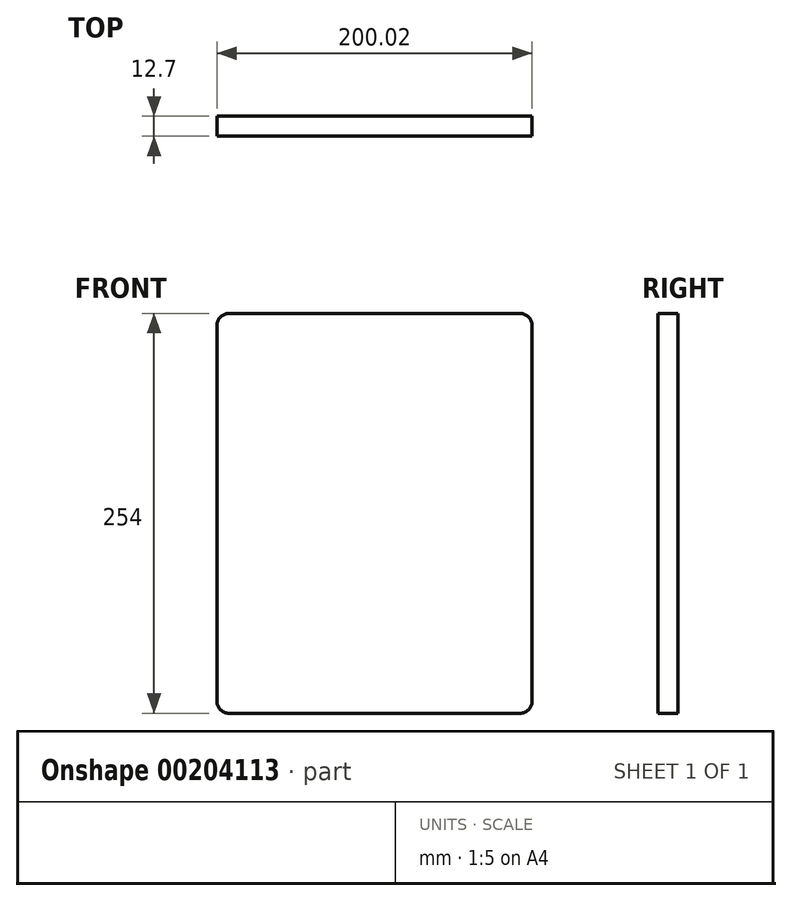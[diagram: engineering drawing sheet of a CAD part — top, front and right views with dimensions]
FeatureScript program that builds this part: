
annotation { "Feature Type Name" : "Feature", "Feature Type Description" : "" }
export const myFeature = defineFeature(function(context is Context, id is Id, definition is map)
    precondition{}
    {
        {
            var Q0;
            Q0=qCreatedBy(makeId("Front.planeOp"),FACE);
            var sketch = newSketch(context, id + "F0", { "sketchPlane" : qUnion([Q0])});
            skLineSegment(sketch, "E0.bottom", {"start": v(-100.01, 127) * mm, "end": v(100.01, 127) * mm});
            skLineSegment(sketch, "E0.top", {"start": v(-100.01, -127) * mm, "end": v(100.01, -127) * mm});
            skLineSegment(sketch, "E0.left", {"start": v(-100.01, 127) * mm, "end": v(-100.01, -127) * mm});
            skLineSegment(sketch, "E0.right", {"start": v(100.01, 127) * mm, "end": v(100.01, -127) * mm});
            skLineSegment(sketch, "E1", {"start": v(0, 127) * mm, "end": v(0, -127) * mm, "construction": true});
            skLineSegment(sketch, "E2", {"start": v(-100.01, 0) * mm, "end": v(100.01, 0) * mm, "construction": true});
            skSolve(sketch);
        }
        {
            var Q0;
            Q0 = qSketchRegion(id + "F0", true);
            extrude(context, id + "F1", {"entities" : qUnion([Q0]), "depth" : 12.7 * mm});
        }
        {
            var Q0;
            Q0=makeQuery(id+"F1.opExtrude","SWEPT_EDGE",EDGE,{"disambiguationData":[OSD([sQuery(id+"F0.wireOp",EDGE,"E0.bottom"),sQuery(id+"F0.wireOp",EDGE,"E0.right")])]});
            var Q1;
            Q1=makeQuery(id+"F1.opExtrude","SWEPT_EDGE",EDGE,{"disambiguationData":[OSD([sQuery(id+"F0.wireOp",EDGE,"E0.bottom"),sQuery(id+"F0.wireOp",EDGE,"E0.left")])]});
            var Q2;
            Q2=makeQuery(id+"F1.opExtrude","SWEPT_EDGE",EDGE,{"disambiguationData":[OSD([sQuery(id+"F0.wireOp",EDGE,"E0.top"),sQuery(id+"F0.wireOp",EDGE,"E0.right")])]});
            var Q3;
            Q3=makeQuery(id+"F1.opExtrude","SWEPT_EDGE",EDGE,{"disambiguationData":[OSD([sQuery(id+"F0.wireOp",EDGE,"E0.top"),sQuery(id+"F0.wireOp",EDGE,"E0.left")])]});
            fillet(context, id + "F2", {"entities" : qUnion([Q0, Q1, Q2, Q3]), "radius" : 7.62 * mm, "tangentPropagation" : true, "allowEdgeOverflow" : false});
        }
    });
